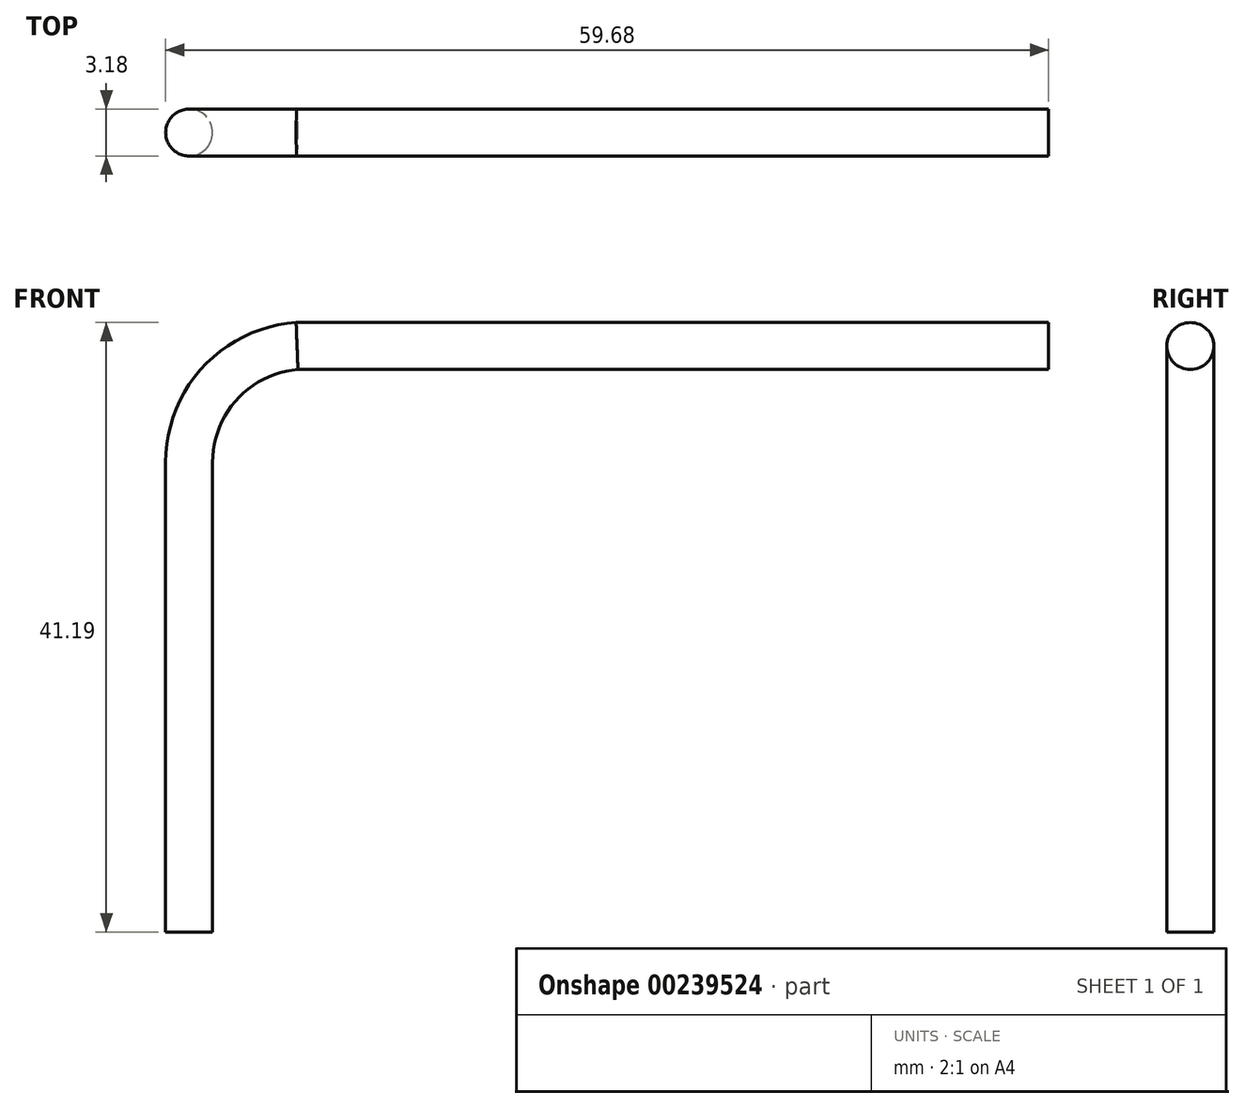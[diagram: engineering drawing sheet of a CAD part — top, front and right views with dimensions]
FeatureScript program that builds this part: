
annotation { "Feature Type Name" : "Feature", "Feature Type Description" : "" }
export const myFeature = defineFeature(function(context is Context, id is Id, definition is map)
    precondition{}
    {
        {
            var Q0;
            Q0=qCreatedBy(makeId("Front.planeOp"),FACE);
            var sketch = newSketch(context, id + "F0", { "sketchPlane" : qUnion([Q0])});
            skLineSegment(sketch, "E0", {"start": v(0, 0) * mm, "end": v(0, 31.75) * mm});
            skArc(sketch, "E1", {"start": v(0, 31.75) * mm, "mid": v(2.1, 37.1) * mm, "end": v(7.3, 39.6) * mm});
            skLineSegment(sketch, "E2", {"start": v(7.3, 39.6) * mm, "end": v(58.1, 39.6) * mm});
            skSolve(sketch);
        }
        {
            var Q0;
            Q0=qCreatedBy(makeId("Top.planeOp"),FACE);
            var sketch = newSketch(context, id + "F1", { "sketchPlane" : qUnion([Q0])});
            skCircle(sketch, "E3", {"center": v(0, 0) * mm, "radius": 1.59 * mm});
            skSolve(sketch);
        }
        {
            var Q0;
            Q0=makeQuery(id+"F1.imprint","IMPRINT",FACE,{"disambiguationData":[TD([[makeQuery(id+"F1.imprint","IMPRINT",EDGE,{"derivedFrom":sQuery(id+"F1.wireOp",EDGE,"E3")}),1.0]])]});
            var Q1;
            Q1=sQuery(id+"F0.wireOp",EDGE,"E0");
            var Q2;
            Q2=sQuery(id+"F0.wireOp",EDGE,"E1");
            var Q3;
            Q3=sQuery(id+"F0.wireOp",EDGE,"E2");
            sweep(context, id + "F2", {"profiles" : qUnion([Q0]), "path" : qUnion([Q1, Q2, Q3])});
        }
    });
